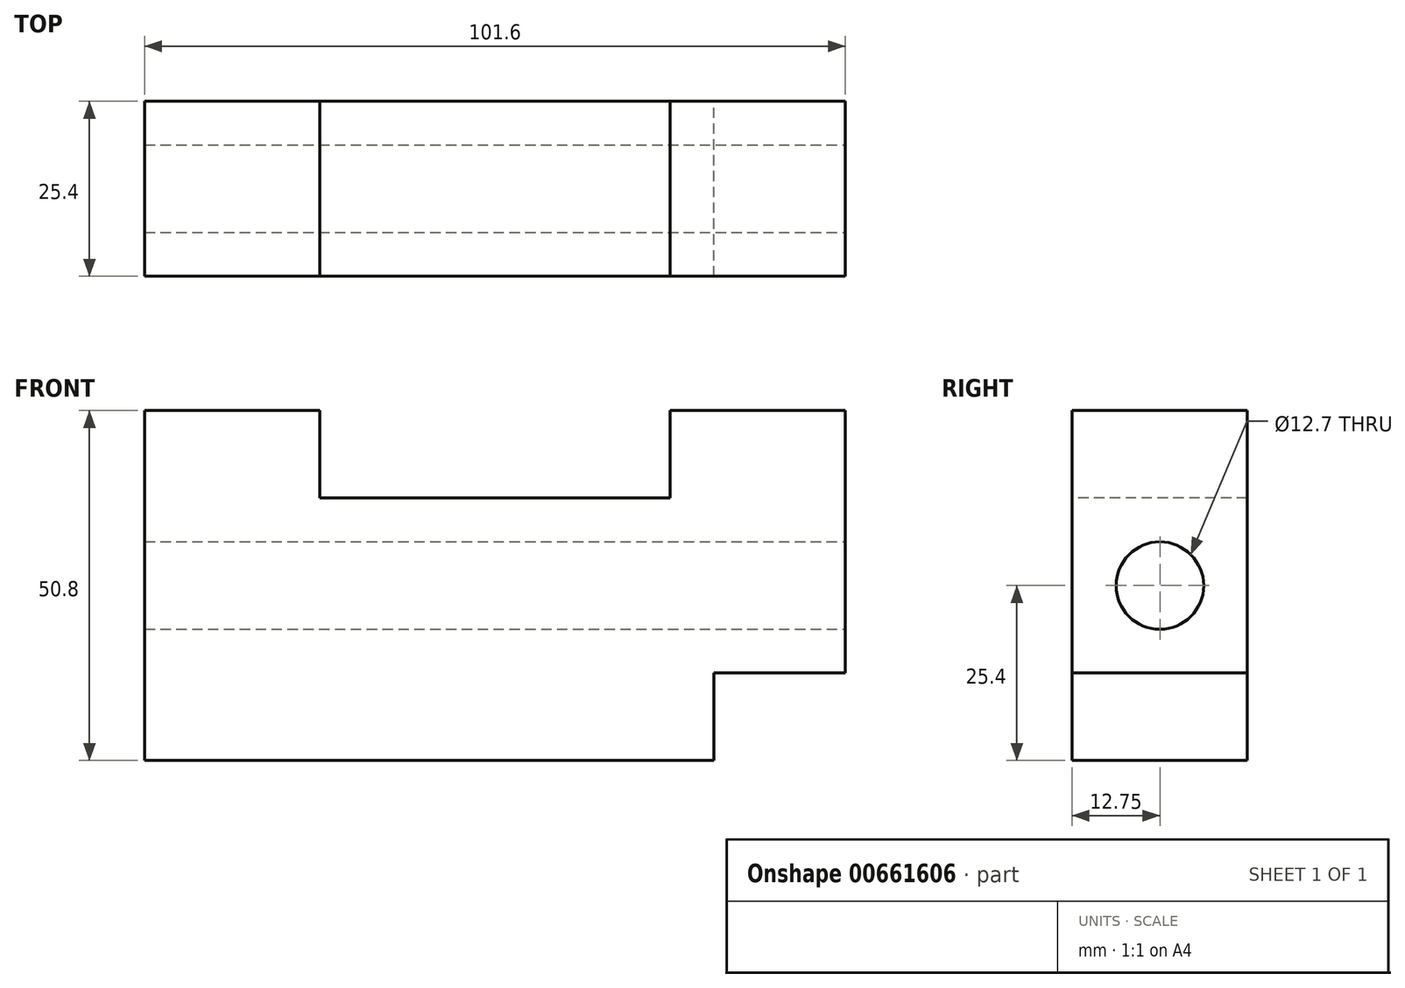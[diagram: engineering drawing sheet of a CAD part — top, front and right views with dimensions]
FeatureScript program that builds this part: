
annotation { "Feature Type Name" : "Feature", "Feature Type Description" : "" }
export const myFeature = defineFeature(function(context is Context, id is Id, definition is map)
    precondition{}
    {
        {
            var Q0;
            Q0=qCreatedBy(makeId("Front.planeOp"),FACE);
            var sketch = newSketch(context, id + "F0", { "sketchPlane" : qUnion([Q0])});
            skLineSegment(sketch, "E0.bottom", {"start": v(-49.67, 25.4) * mm, "end": v(51.93, 25.4) * mm});
            skLineSegment(sketch, "E0.top", {"start": v(-49.67, -25.4) * mm, "end": v(51.93, -25.4) * mm});
            skLineSegment(sketch, "E0.left", {"start": v(-49.67, 25.4) * mm, "end": v(-49.67, -25.4) * mm});
            skLineSegment(sketch, "E0.right", {"start": v(51.93, 25.4) * mm, "end": v(51.93, -25.4) * mm});
            skPoint(sketch, "E0.middle", {"position": v(1.13, 0) * mm});
            skSolve(sketch);
        }
        {
            var Q0;
            Q0 = qSketchRegion(id + "F0", true);
            extrude(context, id + "F1", {"entities" : qUnion([Q0]), "depth" : 25.4 * mm, "offsetDistance" : 25.4 * mm});
        }
        {
            var Q0;
            Q0=makeQuery(id+"F1.opExtrude","CAP_FACE",FACE,{"disambiguationData":[OSD([sQuery(id+"F0.wireOp",EDGE,"E0.bottom"),sQuery(id+"F0.wireOp",EDGE,"E0.top"),sQuery(id+"F0.wireOp",EDGE,"E0.left"),sQuery(id+"F0.wireOp",EDGE,"E0.right")])],"isStart":false});
            var sketch = newSketch(context, id + "F2", { "sketchPlane" : qUnion([Q0])});
            skLineSegment(sketch, "E1.bottom", {"start": v(-24.27, 25.4) * mm, "end": v(26.53, 25.4) * mm});
            skLineSegment(sketch, "E1.top", {"start": v(-24.27, 12.7) * mm, "end": v(26.53, 12.7) * mm});
            skLineSegment(sketch, "E1.left", {"start": v(-24.27, 25.4) * mm, "end": v(-24.27, 12.7) * mm});
            skLineSegment(sketch, "E1.right", {"start": v(26.53, 25.4) * mm, "end": v(26.53, 12.7) * mm});
            skSolve(sketch);
        }
        {
            var Q0;
            Q0=makeQuery(id+"F2.imprint","IMPRINT",FACE,{"disambiguationData":[TD([[makeQuery(id+"F2.imprint","IMPRINT",EDGE,{"derivedFrom":sQuery(id+"F2.wireOp",EDGE,"E1.bottom")}),-1.0]])]});
            extrude(context, id + "F3", {"entities" : qUnion([Q0]), "operationType" : NewBodyOperationType.REMOVE, "endBound" : BoundingType.THROUGH_ALL, "oppositeDirection" : true, "depth" : 25.4 * mm, "offsetDistance" : 25.4 * mm});
        }
        {
            var Q0;
            Q0=makeQuery(id+"F1.opExtrude","SWEPT_FACE",FACE,{"disambiguationData":[OSD([sQuery(id+"F0.wireOp",EDGE,"E0.right")])]});
            var sketch = newSketch(context, id + "F4", { "sketchPlane" : qUnion([Q0])});
            skLineSegment(sketch, "E2.bottom", {"start": v(-25.4, -25.4) * mm, "end": v(0, -25.4) * mm});
            skLineSegment(sketch, "E2.top", {"start": v(-25.4, -12.7) * mm, "end": v(0, -12.7) * mm});
            skLineSegment(sketch, "E2.left", {"start": v(-25.4, -25.4) * mm, "end": v(-25.4, -12.7) * mm});
            skLineSegment(sketch, "E2.right", {"start": v(0, -25.4) * mm, "end": v(0, -12.7) * mm});
            skSolve(sketch);
        }
        {
            var Q0;
            Q0=makeQuery(id+"F4.imprint","IMPRINT",FACE,{"disambiguationData":[TD([[makeQuery(id+"F4.imprint","IMPRINT",EDGE,{"derivedFrom":sQuery(id+"F4.wireOp",EDGE,"E2.bottom")}),1.0]])]});
            extrude(context, id + "F5", {"entities" : qUnion([Q0]), "operationType" : NewBodyOperationType.REMOVE, "oppositeDirection" : true, "depth" : 19.05 * mm, "offsetDistance" : 25.4 * mm});
        }
        {
            var Q0;
            Q0=makeQuery(id+"F1.opExtrude","SWEPT_FACE",FACE,{"disambiguationData":[OSD([sQuery(id+"F0.wireOp",EDGE,"E0.right")])]});
            var sketch = newSketch(context, id + "F6", { "sketchPlane" : qUnion([Q0])});
            skCircle(sketch, "E3", {"center": v(-12.65, 0) * mm, "radius": 6.35 * mm});
            skSolve(sketch);
        }
        {
            var Q0;
            Q0=makeQuery(id+"F6.imprint","IMPRINT",FACE,{"disambiguationData":[TD([[makeQuery(id+"F6.imprint","IMPRINT",EDGE,{"derivedFrom":sQuery(id+"F6.wireOp",EDGE,"E3")}),1.0]])]});
            extrude(context, id + "F7", {"entities" : qUnion([Q0]), "operationType" : NewBodyOperationType.REMOVE, "endBound" : BoundingType.THROUGH_ALL, "oppositeDirection" : true, "depth" : 25.4 * mm, "offsetDistance" : 25.4 * mm});
        }
    });
